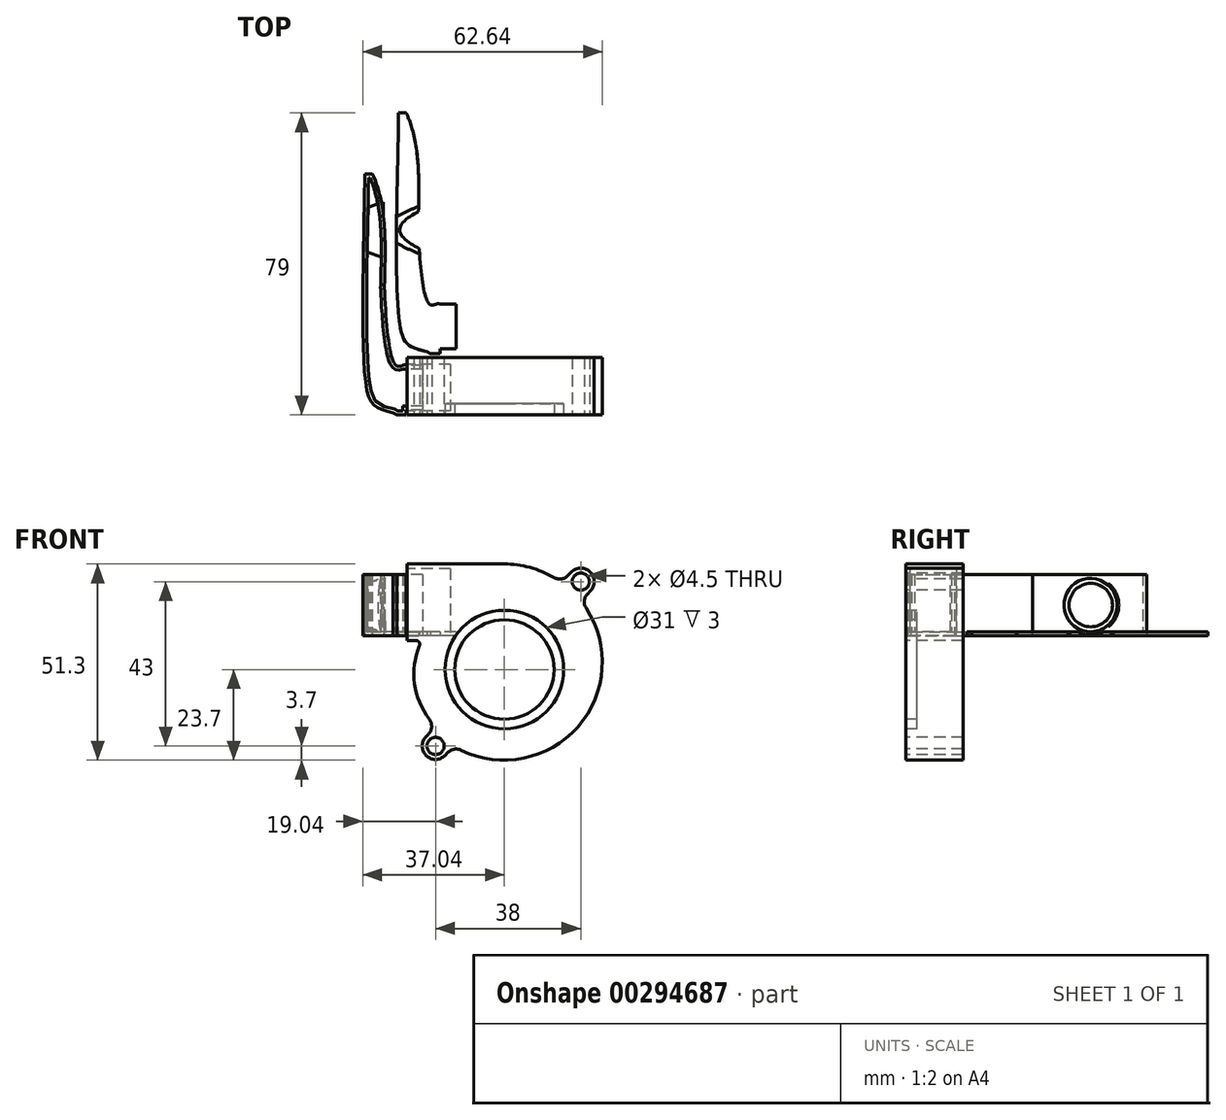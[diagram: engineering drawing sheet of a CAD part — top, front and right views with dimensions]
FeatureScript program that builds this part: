
annotation { "Feature Type Name" : "Feature", "Feature Type Description" : "" }
export const myFeature = defineFeature(function(context is Context, id is Id, definition is map)
    precondition{}
    {
        {
            assignVariable(context, id + "F0", {"name" : "tol", "anyValue" : .25});
        }
        {
            var Q0;
            Q0=qCreatedBy(makeId("Front.planeOp"),FACE);
            var sketch = newSketch(context, id + "F1", { "sketchPlane" : qUnion([Q0])});
            skLineSegment(sketch, "E0", {"start": v(0, 39.18) * mm, "end": v(0, -45.98) * mm, "construction": true});
            skLineSegment(sketch, "E1", {"start": v(-59.51, 0) * mm, "end": v(60.38, 0) * mm, "construction": true});
            skCircle(sketch, "E2", {"center": v(0, 0) * mm, "radius": 13 * mm});
            skCircle(sketch, "E3", {"center": v(0, 0) * mm, "radius": 15.5 * mm});
            skCircle(sketch, "E4", {"center": v(20, 23) * mm, "radius": 2.25 * mm});
            skCircle(sketch, "E5", {"center": v(-18, -20) * mm, "radius": 2.25 * mm});
            skLineSegment(sketch, "E6.bottom", {"start": v(-25.4, 27.6) * mm, "end": v(0, 27.6) * mm});
            skLineSegment(sketch, "E6.top", {"start": v(-25.4, 7.6) * mm, "end": v(-21.61, 7.6) * mm});
            skLineSegment(sketch, "E6.left", {"start": v(-25.4, 27.6) * mm, "end": v(-25.4, 7.6) * mm});
            skLineSegment(sketch, "E7", {"start": v(-62.06, -23.7) * mm, "end": v(66.72, -23.7) * mm, "construction": true});
            skArc(sketch, "E8", {"start": v(-13.15, -20.1) * mm, "mid": v(19.31, -14.88) * mm, "end": v(19.95, 18) * mm});
            skArc(sketch, "E9", {"start": v(-20.47, -17.53) * mm, "mid": v(-20.47, -22.47) * mm, "end": v(-15.53, -22.47) * mm});
            skArc(sketch, "E10", {"start": v(22.47, 20.53) * mm, "mid": v(22.47, 25.47) * mm, "end": v(17.53, 25.47) * mm});
            skLineSegment(sketch, "E11", {"start": v(17.53, 25.47) * mm, "end": v(14.86, 22.81) * mm});
            skLineSegment(sketch, "E12", {"start": v(22.47, 20.53) * mm, "end": v(19.95, 18) * mm});
            skLineSegment(sketch, "E13", {"start": v(-20.47, -17.53) * mm, "end": v(-17.92, -14.97) * mm});
            skLineSegment(sketch, "E14", {"start": v(-15.53, -22.47) * mm, "end": v(-13.15, -20.1) * mm});
            skArc(sketch, "E15.trimOffspring", {"start": v(14.86, 22.81) * mm, "mid": v(7.78, 26.37) * mm, "end": v(-0.05, 27.6) * mm});
            skArc(sketch, "E16", {"start": v(-21.61, 7.6) * mm, "mid": v(-23.4, -4.28) * mm, "end": v(-17.92, -14.97) * mm});
            skSolve(sketch);
        }
        {
            var Q0;
            Q0=makeQuery(id+"F1.imprint","IMPRINT",FACE,{"disambiguationData":[TD([[makeQuery(id+"F1.imprint","IMPRINT",EDGE,{"derivedFrom":sQuery(id+"F1.wireOp",EDGE,"E3")}),-1.0]])]});
            var Q1;
            Q1=makeQuery(id+"F1.imprint","IMPRINT",FACE,{"disambiguationData":[TD([[makeQuery(id+"F1.imprint","IMPRINT",EDGE,{"derivedFrom":sQuery(id+"F1.wireOp",EDGE,"E2")}),1.0]])]});
            var Q2;
            Q2=makeQuery(id+"F1.imprint","IMPRINT",FACE,{"disambiguationData":[TD([[makeQuery(id+"F1.imprint","IMPRINT",EDGE,{"derivedFrom":sQuery(id+"F1.wireOp",EDGE,"E2")}),-1.0]])]});
            extrude(context, id + "F2", {"entities" : qUnion([Q0, Q1, Q2]), "oppositeDirection" : true, "depth" : 15 * mm});
        }
        {
            var Q0;
            Q0=makeQuery(id+"F1.imprint","IMPRINT",FACE,{"disambiguationData":[TD([[makeQuery(id+"F1.imprint","IMPRINT",EDGE,{"derivedFrom":sQuery(id+"F1.wireOp",EDGE,"E2")}),-1.0]])]});
            extrude(context, id + "F3", {"entities" : qUnion([Q0]), "operationType" : NewBodyOperationType.REMOVE, "oppositeDirection" : true, "depth" : 3 * mm});
        }
        {
            var Q0;
            Q0=makeQuery(id+"F2.opExtrude","SWEPT_FACE",FACE,{"disambiguationData":[OSD([sQuery(id+"F1.wireOp",EDGE,"E6.left")])]});
            var sketch = newSketch(context, id + "F4", { "sketchPlane" : qUnion([Q0])});
            skLineSegment(sketch, "E17.bottom", {"start": v(-13.2, 26.4) * mm, "end": v(-1, 26.4) * mm});
            skLineSegment(sketch, "E17.top", {"start": v(-13.2, 8.8) * mm, "end": v(-1, 8.8) * mm});
            skLineSegment(sketch, "E17.left", {"start": v(-13.2, 26.4) * mm, "end": v(-13.2, 8.8) * mm});
            skLineSegment(sketch, "E17.right", {"start": v(-1, 26.4) * mm, "end": v(-1, 8.8) * mm});
            skLineSegment(sketch, "E18", {"start": v(13.3, 0) * mm, "end": v(-29.9, 0) * mm, "construction": true});
            skSolve(sketch);
        }
        {
            var Q0;
            Q0 = qSketchRegion(id + "F4", true);
            extrude(context, id + "F5", {"entities" : qUnion([Q0]), "operationType" : NewBodyOperationType.REMOVE, "oppositeDirection" : true, "depth" : 11.3 * mm});
        }
        {
            var Q0;
            Q0=makeQuery(id+"F2.opExtrude","SWEPT_EDGE",EDGE,{"disambiguationData":[OSD([sQuery(id+"F1.wireOp",EDGE,"E6.top"),sQuery(id+"F1.wireOp",EDGE,"E16")])]});
            fillet(context, id + "F6", {"entities" : qUnion([Q0]), "radius" : 1 * mm, "tangentPropagation" : true, "allowEdgeOverflow" : false});
        }
        {
            var Q0;
            Q0=makeQuery(id+"F2.opExtrude","SWEPT_EDGE",EDGE,{"disambiguationData":[OSD([sQuery(id+"F1.wireOp",EDGE,"E13"),sQuery(id+"F1.wireOp",EDGE,"E16")])]});
            var Q1;
            Q1=makeQuery(id+"F2.opExtrude","SWEPT_EDGE",EDGE,{"disambiguationData":[OSD([sQuery(id+"F1.wireOp",EDGE,"E8"),sQuery(id+"F1.wireOp",EDGE,"E14")])]});
            var Q2;
            Q2=makeQuery(id+"F2.opExtrude","SWEPT_EDGE",EDGE,{"disambiguationData":[OSD([sQuery(id+"F1.wireOp",EDGE,"E8"),sQuery(id+"F1.wireOp",EDGE,"E12")])]});
            var Q3;
            Q3=makeQuery(id+"F2.opExtrude","SWEPT_EDGE",EDGE,{"disambiguationData":[OSD([sQuery(id+"F1.wireOp",EDGE,"E11"),sQuery(id+"F1.wireOp",EDGE,"E15.trimOffspring")])]});
            fillet(context, id + "F7", {"entities" : qUnion([Q0, Q1, Q2, Q3]), "radius" : 3 * mm, "tangentPropagation" : true, "allowEdgeOverflow" : false});
        }
        {
            var Q0;
            Q0=qCreatedBy(makeId("Top.planeOp"),FACE);
            cPlane(context, id + "F8", {"entities" : qUnion([Q0]), "cplaneType" : CPlaneType.OFFSET, "offset" : 8.8 * mm, "width" : 150 * mm, "height" : 150 * mm});
        }
        {
            var Q0;
            Q0=qCreatedBy(id+"F8.planeOp",FACE);
            var sketch = newSketch(context, id + "F9", { "sketchPlane" : qUnion([Q0])});
            skLineSegment(sketch, "E19.bottom", {"start": v(-21.4, 12.95) * mm, "end": v(-25.65, 12.95) * mm});
            skLineSegment(sketch, "E19.top", {"start": v(-21.4, 1.25) * mm, "end": v(-25.65, 1.25) * mm});
            skLineSegment(sketch, "E19.left", {"start": v(-21.4, 12.95) * mm, "end": v(-21.4, 1.25) * mm});
            skLineSegment(sketch, "E19.right", {"start": v(-25.65, 12.95) * mm, "end": v(-25.65, 1.25) * mm});
            skFitSpline(sketch, "E20", {"points": [v(-25.65, 12.95) * mm, v(-28.3, 12.88) * mm, v(-31.69, 63) * mm], "startDerivative": vector(-10.33, 8.63) * mm, "endDerivative": vector(0.1, 33.27) * mm});
            skFitSpline(sketch, "E21", {"points": [v(-25.65, 1.25) * mm, v(-31.69, 1.25) * mm, v(-36.13, 7.45) * mm, v(-36.53, 63) * mm], "startDerivative": vector(-5.48, -23.08) * mm, "endDerivative": vector(-0.64, 49.33) * mm});
            skLineSegment(sketch, "E22", {"start": v(-34.52, 63) * mm, "end": v(-35.53, 63) * mm});
            skFitSpline(sketch, "E23", {"points": [v(-34.52, 63) * mm, v(-31.72, 52.95) * mm, v(-31.3, 32.18) * mm], "startDerivative": vector(1.95, -2.22) * mm, "endDerivative": vector(1.47, -4.31) * mm});
            skLineSegment(sketch, "E24", {"start": v(-35.53, 63) * mm, "end": v(-36.53, 63) * mm});
            skLineSegment(sketch, "E25", {"start": v(-25.65, 12.89) * mm, "end": v(-25.65, 12.95) * mm});
            skLineSegment(sketch, "E26", {"start": v(-25.65, 12.89) * mm, "end": v(-26.85, 12.89) * mm});
            skLineSegment(sketch, "E27", {"start": v(-25.65, 1.25) * mm, "end": v(-25.65, 0) * mm});
            skLineSegment(sketch, "E28", {"start": v(-25.65, 0) * mm, "end": v(-28.15, 0) * mm});
            skLineSegment(sketch, "E29", {"start": v(-28.15, 0) * mm, "end": v(-29.08, 0.54) * mm});
            skLineSegment(sketch, "E30", {"start": v(-37.35, 48.74) * mm, "end": v(-37.35, -19.9) * mm, "construction": true});
            skSolve(sketch);
        }
        {
            var Q0;
            Q0 = qSketchRegion(id + "F9", true);
            extrude(context, id + "F10", {"entities" : qUnion([Q0]), "depth" : (16.6 - getVariable(context, 'tol') * 2) * mm});
        }
        {
            var Q0;
            Q0=makeQuery(id+"F10.opExtrude","CAP_FACE",FACE,{"disambiguationData":[OSD([sQuery(id+"F9.wireOp",EDGE,"E19.bottom"),sQuery(id+"F9.wireOp",EDGE,"E19.top"),sQuery(id+"F9.wireOp",EDGE,"E19.left"),sQuery(id+"F9.wireOp",EDGE,"E20"),sQuery(id+"F9.wireOp",EDGE,"E21"),sQuery(id+"F9.wireOp",EDGE,"E22"),sQuery(id+"F9.wireOp",EDGE,"E23"),sQuery(id+"F9.wireOp",EDGE,"E24"),sQuery(id+"F9.wireOp",EDGE,"E25"),sQuery(id+"F9.wireOp",EDGE,"E26"),sQuery(id+"F9.wireOp",EDGE,"E27"),sQuery(id+"F9.wireOp",EDGE,"E28"),sQuery(id+"F9.wireOp",EDGE,"E29")])],"isStart":false});
            shell(context, id + "F11", {"entities" : qUnion([Q0]), "thickness" : 1 * mm});
        }
        {
            var Q0;
            Q0 = qSketchRegion(id + "F9", true);
            extrude(context, id + "F12", {"entities" : qUnion([Q0]), "depth" : 1 * mm});
        }
        {
            var Q0;
            Q0=makeQuery(id+"F12.opExtrude","SWEPT_BODY",BODY,{"disambiguationData":[OSD([sQuery(id+"F9.wireOp",EDGE,"E19.bottom"),sQuery(id+"F9.wireOp",EDGE,"E19.top"),sQuery(id+"F9.wireOp",EDGE,"E19.left"),sQuery(id+"F9.wireOp",EDGE,"E20"),sQuery(id+"F9.wireOp",EDGE,"E21"),sQuery(id+"F9.wireOp",EDGE,"E22"),sQuery(id+"F9.wireOp",EDGE,"E23"),sQuery(id+"F9.wireOp",EDGE,"E24"),sQuery(id+"F9.wireOp",EDGE,"E25"),sQuery(id+"F9.wireOp",EDGE,"E26"),sQuery(id+"F9.wireOp",EDGE,"E27"),sQuery(id+"F9.wireOp",EDGE,"E28"),sQuery(id+"F9.wireOp",EDGE,"E29")])]});
            transform(context, id + "F13", {"entities" : qUnion([Q0]), "transformType" : TransformType.TRANSLATION_3D, "dx" : 8.8 * mm, "dy" : 16 * mm, "dz" : 0 * mm, "makeCopy" : false});
        }
        {
            var Q0;
            Q0=makeQuery(id+"F10.opExtrude","SWEPT_FACE",FACE,{"disambiguationData":[OSD([sQuery(id+"F9.wireOp",EDGE,"E19.left")])]});
            var sketch = newSketch(context, id + "F14", { "sketchPlane" : qUnion([Q0])});
            skLineSegment(sketch, "E31.bottom", {"start": v(11.95, 24.9) * mm, "end": v(2.25, 24.9) * mm});
            skLineSegment(sketch, "E31.top", {"start": v(11.95, 9.8) * mm, "end": v(2.25, 9.8) * mm});
            skLineSegment(sketch, "E31.left", {"start": v(11.95, 24.9) * mm, "end": v(11.95, 9.8) * mm});
            skLineSegment(sketch, "E31.right", {"start": v(2.25, 24.9) * mm, "end": v(2.25, 9.8) * mm});
            skLineSegment(sketch, "E32", {"start": v(11.95, 17.35) * mm, "end": v(12.95, 17.35) * mm, "construction": true});
            skLineSegment(sketch, "E33", {"start": v(2.25, 17.35) * mm, "end": v(1.25, 17.35) * mm, "construction": true});
            skLineSegment(sketch, "E34", {"start": v(7.1, 9.8) * mm, "end": v(7.1, 8.8) * mm, "construction": true});
            skSolve(sketch);
        }
        {
            var Q0;
            Q0 = qSketchRegion(id + "F14", true);
            extrude(context, id + "F15", {"entities" : qUnion([Q0]), "operationType" : NewBodyOperationType.REMOVE, "endBound" : BoundingType.UP_TO_NEXT, "oppositeDirection" : true, "depth" : 25 * mm});
        }
        {
            var Q0;
            Q0=makeQuery(id+"F10.opExtrude","SWEPT_FACE",FACE,{"disambiguationData":[OSD([sQuery(id+"F9.wireOp",EDGE,"E24")])]});
            var sketch = newSketch(context, id + "F16", { "sketchPlane" : qUnion([Q0])});
            skLineSegment(sketch, "E35.bottom", {"start": v(36.48, 24.9) * mm, "end": v(55.33, 24.9) * mm});
            skLineSegment(sketch, "E35.top", {"start": v(36.48, 9.8) * mm, "end": v(55.33, 9.8) * mm});
            skLineSegment(sketch, "E35.left", {"start": v(36.48, 24.9) * mm, "end": v(36.48, 9.8) * mm});
            skLineSegment(sketch, "E35.right", {"start": v(55.33, 24.9) * mm, "end": v(55.33, 9.8) * mm});
            skPoint(sketch, "E36.oppositeSnap0", {"position": v(36.53, 16.85) * mm});
            skLineSegment(sketch, "E36.bottom", {"start": v(36.48, 16.85) * mm, "end": v(36.53, 16.85) * mm, "construction": true});
            skLineSegment(sketch, "E36.left", {"start": v(36.53, 16.85) * mm, "end": v(36.53, 16.85) * mm});
            skLineSegment(sketch, "E36.right", {"start": v(36.48, 16.85) * mm, "end": v(36.48, 16.85) * mm});
            skLineSegment(sketch, "E37", {"start": v(-28.84, 9.8) * mm, "end": v(-28.84, 8.8) * mm, "construction": true});
            skLineSegment(sketch, "E38", {"start": v(35.53, 16.85) * mm, "end": v(36.53, 16.85) * mm, "construction": true});
            skSolve(sketch);
        }
        {
            var Q0;
            Q0=qCreatedBy(makeId("Right.planeOp"),FACE);
            cPlane(context, id + "F17", {"entities" : qUnion([Q0]), "cplaneType" : CPlaneType.OFFSET, "offset" : 36.2 * mm, "oppositeDirection" : true, "width" : 150 * mm, "height" : 150 * mm});
        }
        {
            var Q0;
            Q0=qCreatedBy(id+"F17.planeOp",FACE);
            var sketch = newSketch(context, id + "F18", { "sketchPlane" : qUnion([Q0])});
            skCircle(sketch, "E39", {"center": v(48.4, 16.85) * mm, "radius": 5.68 * mm});
            skLineSegment(sketch, "E40", {"start": v(27.58, 16.85) * mm, "end": v(56.22, 16.85) * mm, "construction": true});
            skSolve(sketch);
        }
        {
            var Q0;
            Q0 = qSketchRegion(id + "F18", true);
            var Q1;
            Q1=sQuery(id+"F9.wireOp",VERTEX,"E23.1.internal");
            extrude(context, id + "F19", {"entities" : qUnion([Q0]), "operationType" : NewBodyOperationType.ADD, "endBound" : BoundingType.UP_TO_VERTEX, "endBoundEntityVertex" : qUnion([Q1]), "depth" : 25 * mm, "hasDraft" : true, "draftAngle" : 20 * degree});
        }
        {
            var Q0;
            Q0 = qSketchRegion(id + "F18", true);
            extrude(context, id + "F20", {"entities" : qUnion([Q0]), "operationType" : NewBodyOperationType.REMOVE, "depth" : 25 * mm, "hasDraft" : true, "draftAngle" : 15 * degree});
        }
    });
